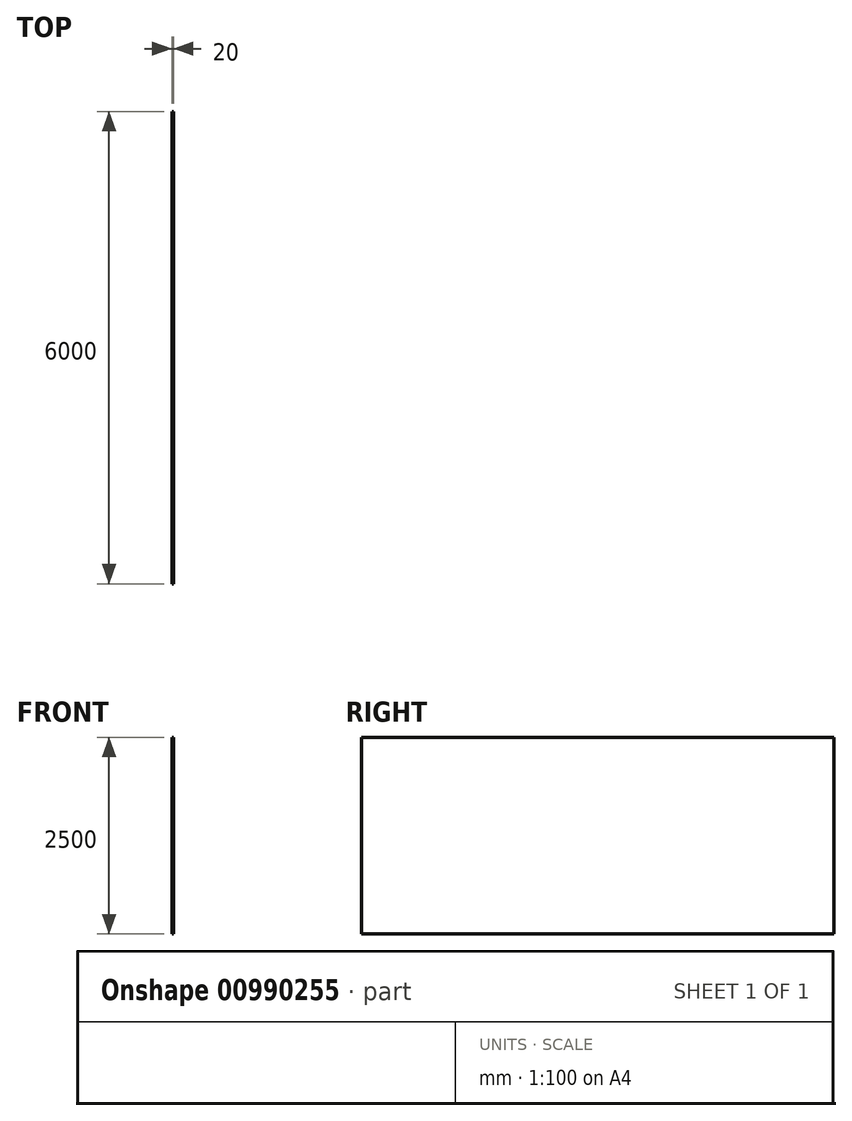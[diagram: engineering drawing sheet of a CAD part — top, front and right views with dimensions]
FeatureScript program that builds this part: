
annotation { "Feature Type Name" : "Feature", "Feature Type Description" : "" }
export const myFeature = defineFeature(function(context is Context, id is Id, definition is map)
    precondition{}
    {
        {
            var Q0;
            Q0=qCreatedBy(makeId("Right.planeOp"),FACE);
            var sketch = newSketch(context, id + "F0", { "sketchPlane" : qUnion([Q0])});
            skLineSegment(sketch, "E0.bottom", {"start": v(-2526.63, 1249.7) * mm, "end": v(3473.37, 1249.7) * mm});
            skLineSegment(sketch, "E0.top", {"start": v(-2526.63, -1250.3) * mm, "end": v(3473.37, -1250.3) * mm});
            skLineSegment(sketch, "E0.left", {"start": v(-2526.63, 1249.7) * mm, "end": v(-2526.63, -1250.3) * mm});
            skLineSegment(sketch, "E0.right", {"start": v(3473.37, 1249.7) * mm, "end": v(3473.37, -1250.3) * mm});
            skSolve(sketch);
        }
        {
            var Q0;
            Q0=makeQuery(id+"F0.imprint","IMPRINT",FACE,{"disambiguationData":[TD([[makeQuery(id+"F0.imprint","IMPRINT",EDGE,{"derivedFrom":sQuery(id+"F0.wireOp",EDGE,"E0.bottom")}),-1.0]])]});
            extrude(context, id + "F1", {"entities" : qUnion([Q0]), "depth" : 20 * mm, "offsetDistance" : 25 * mm});
        }
    });
